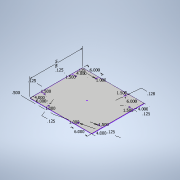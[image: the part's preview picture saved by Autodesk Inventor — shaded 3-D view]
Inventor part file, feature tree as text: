
AUTODESK INVENTOR PART (.ipt)
format: ipt  version: 2021 (Build 250183000, 183)  size: 172,032 bytes
history: native  units: in
note: dims shown in document units (in); Inventor stores cm internally (conversion verified against a paired STEP export)
features: sketch x4, other x2, extrude x2
ambient origin geometry x8: Origin, YZ Plane, XZ Plane, XY Plane, X Axis, Y Axis, Z Axis, Center Point
bodies: Solid1 (feature_tree)
feature tree (8):
  other  "Annotations"
  extrude  "Extrusion1"  Depth=19.6in
  sketch  "Sketch3"  dims[d2=0.06in d3=0.0in d10=4.0in]
  extrude  "Extrusion3"  Depth=0.06in
  sketch  "Sketch5"  dims[d12=0.5in d13=4.0in d14=1.5in d15=0.5in d16=6.0in d18=0.5in d19=6.0in d20=1.5in d21=0.5in d22=4.0in d23=1.5in d24=4.0in d25=1.5in d26=6.0in d27=1.0in d28=0.5in d29=6.0in d30=1.0in d31=0.5in d32=0.5in d33=0.5in d34=1.0in d35=0.0in d39=1.0in d42=4.0in d43=1.5in d44=0.125in d45=4.0in d46=1.5in d47=0.125in d48=6.0in d49=0.125in d50=6.0in d51=1.5in d52=0.128in d53=4.0in d54=1.5in d55=4.0in d56=1.5in d57=6.0in d58=1.0in d59=0.5in d60=6.0in d61=1.0in d62=0.125in d63=0.125in d64=0.125in d65=1.0in d36=0.0in d37=0.3937in d38=19.6in]
  sketch  "Sketch1"  dims[d0=23.0in d1=19.6in]
  sketch  "Sketch4"  dims[d11=1.5in]
  other  "Linear Dimension 1"
